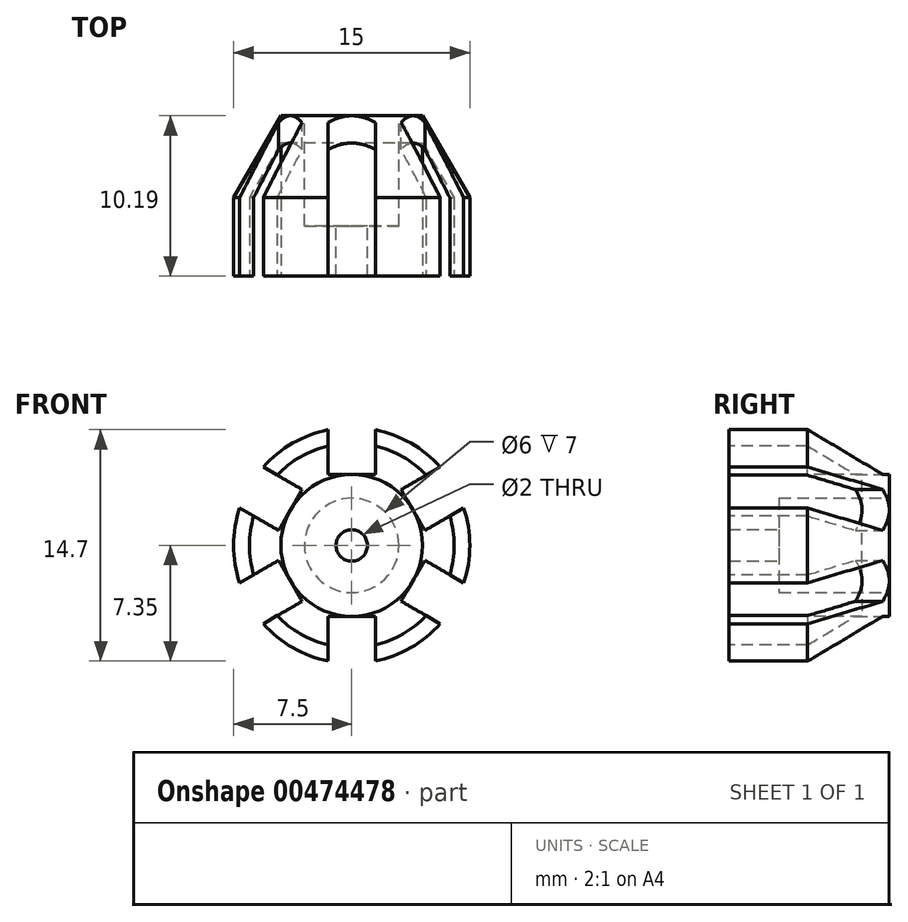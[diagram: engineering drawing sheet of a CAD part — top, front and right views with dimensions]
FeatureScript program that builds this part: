
annotation { "Feature Type Name" : "Feature", "Feature Type Description" : "" }
export const myFeature = defineFeature(function(context is Context, id is Id, definition is map)
    precondition{}
    {
        {
            var Q0;
            Q0=qCreatedBy(makeId("Right.planeOp"),FACE);
            var sketch = newSketch(context, id + "F0", { "sketchPlane" : qUnion([Q0])});
            skLineSegment(sketch, "E0", {"start": v(16.88, 0) * mm, "end": v(16.88, 4.5) * mm});
            skLineSegment(sketch, "E1", {"start": v(16.88, 4.5) * mm, "end": v(11.69, 7.5) * mm});
            skLineSegment(sketch, "E2", {"start": v(11.69, 7.5) * mm, "end": v(6.69, 7.5) * mm});
            skLineSegment(sketch, "E3", {"start": v(6.69, 7.5) * mm, "end": v(6.69, 6.5) * mm});
            skLineSegment(sketch, "E4", {"start": v(6.69, 6.5) * mm, "end": v(11.69, 6.5) * mm});
            skLineSegment(sketch, "E5", {"start": v(11.69, 6.5) * mm, "end": v(15.15, 4.5) * mm});
            skLineSegment(sketch, "E6", {"start": v(15.15, 4.5) * mm, "end": v(6.69, 4.5) * mm});
            skLineSegment(sketch, "E7", {"start": v(6.69, 4.5) * mm, "end": v(6.69, 0) * mm});
            skLineSegment(sketch, "E8", {"start": v(6.69, 0) * mm, "end": v(16.88, 0) * mm});
            skLineSegment(sketch, "E9", {"start": v(0, 0) * mm, "end": v(16.88, 0) * mm, "construction": true});
            skSolve(sketch);
        }
        {
            var Q0;
            Q0 = qSketchRegion(id + "F0", true);
            var Q1;
            Q1=sQuery(id+"F0.wireOp",EDGE,"E9");
            revolve(context, id + "F1", {"entities" : qUnion([Q0]), "axis" : qUnion([Q1]), "revolveType" : RevolveType.FULL});
        }
        {
            var Q0;
            Q0=makeQuery(id+"F1.opRevolve","SWEPT_FACE",FACE,{"disambiguationData":[OSD([sQuery(id+"F0.wireOp",EDGE,"E0")])]});
            var sketch = newSketch(context, id + "F2", { "sketchPlane" : qUnion([Q0])});
            skCircle(sketch, "E10", {"center": v(0, 0) * mm, "radius": 7.5 * mm});
            skLineSegment(sketch, "E11.bottom", {"start": v(-1.5, 10.5) * mm, "end": v(1.5, 10.5) * mm});
            skLineSegment(sketch, "E11.top", {"start": v(-1.5, 4.5) * mm, "end": v(1.5, 4.5) * mm});
            skLineSegment(sketch, "E11.left", {"start": v(-1.5, 10.5) * mm, "end": v(-1.5, 4.5) * mm});
            skLineSegment(sketch, "E11.right", {"start": v(1.5, 10.5) * mm, "end": v(1.5, 4.5) * mm});
            skPoint(sketch, "E11.middle", {"position": v(0, 7.5) * mm});
            skLineSegment(sketch, "E12.1.0", {"start": v(-9.84, 3.95) * mm, "end": v(-4.65, 0.95) * mm});
            skLineSegment(sketch, "E12.1.1", {"start": v(-4.65, 0.95) * mm, "end": v(-3.15, 3.55) * mm});
            skLineSegment(sketch, "E12.1.2", {"start": v(-8.34, 6.55) * mm, "end": v(-3.15, 3.55) * mm});
            skLineSegment(sketch, "E12.1.3", {"start": v(-9.84, 3.95) * mm, "end": v(-8.34, 6.55) * mm});
            skLineSegment(sketch, "E12.2.0", {"start": v(-8.34, -6.55) * mm, "end": v(-3.15, -3.55) * mm});
            skLineSegment(sketch, "E12.2.1", {"start": v(-3.15, -3.55) * mm, "end": v(-4.65, -0.95) * mm});
            skLineSegment(sketch, "E12.2.2", {"start": v(-9.84, -3.95) * mm, "end": v(-4.65, -0.95) * mm});
            skLineSegment(sketch, "E12.2.3", {"start": v(-8.34, -6.55) * mm, "end": v(-9.84, -3.95) * mm});
            skLineSegment(sketch, "E12.3.0", {"start": v(1.5, -10.5) * mm, "end": v(1.5, -4.5) * mm});
            skLineSegment(sketch, "E12.3.1", {"start": v(1.5, -4.5) * mm, "end": v(-1.5, -4.5) * mm});
            skLineSegment(sketch, "E12.3.2", {"start": v(-1.5, -10.5) * mm, "end": v(-1.5, -4.5) * mm});
            skLineSegment(sketch, "E12.3.3", {"start": v(1.5, -10.5) * mm, "end": v(-1.5, -10.5) * mm});
            skLineSegment(sketch, "E12.4.0", {"start": v(9.84, -3.95) * mm, "end": v(4.65, -0.95) * mm});
            skLineSegment(sketch, "E12.4.1", {"start": v(4.65, -0.95) * mm, "end": v(3.15, -3.55) * mm});
            skLineSegment(sketch, "E12.4.2", {"start": v(8.34, -6.55) * mm, "end": v(3.15, -3.55) * mm});
            skLineSegment(sketch, "E12.4.3", {"start": v(9.84, -3.95) * mm, "end": v(8.34, -6.55) * mm});
            skLineSegment(sketch, "E12.5.0", {"start": v(8.34, 6.55) * mm, "end": v(3.15, 3.55) * mm});
            skLineSegment(sketch, "E12.5.1", {"start": v(3.15, 3.55) * mm, "end": v(4.65, 0.95) * mm});
            skLineSegment(sketch, "E12.5.2", {"start": v(9.84, 3.95) * mm, "end": v(4.65, 0.95) * mm});
            skLineSegment(sketch, "E12.5.3", {"start": v(8.34, 6.55) * mm, "end": v(9.84, 3.95) * mm});
            skSolve(sketch);
        }
        {
            var Q0;
            {var subQ0=sQuery(id+"F2.wireOp",EDGE,"E12.2.2");var subQ6=sQuery(id+"F2.wireOp",EDGE,"E10");var subQ7=makeQuery(id+"F2.imprint","INTERSECT",VERTEX,{"derivedFrom":[subQ6,subQ0]});Q0=makeQuery(id+"F2.imprint","IMPRINT",FACE,{"disambiguationData":[TD([[makeQuery(id+"F2.imprint","IMPRINT",EDGE,{"disambiguationData":[TD([[subQ7,-1.0]])],"derivedFrom":subQ6}),1.0]])]});}
            var Q1;
            {var subQ0=sQuery(id+"F2.wireOp",EDGE,"E12.1.2");var subQ6=sQuery(id+"F2.wireOp",EDGE,"E10");var subQ8=makeQuery(id+"F2.imprint","INTERSECT",VERTEX,{"derivedFrom":[subQ6,subQ0]});Q1=makeQuery(id+"F2.imprint","IMPRINT",FACE,{"disambiguationData":[TD([[makeQuery(id+"F2.imprint","IMPRINT",EDGE,{"disambiguationData":[TD([[subQ8,-1.0]])],"derivedFrom":subQ6}),1.0]])]});}
            var Q2;
            {var subQ3=sQuery(id+"F2.wireOp",EDGE,"E10");var subQ5=sQuery(id+"F2.wireOp",EDGE,"E11.right");var subQ8=makeQuery(id+"F2.imprint","INTERSECT",VERTEX,{"derivedFrom":[subQ3,subQ5]});Q2=makeQuery(id+"F2.imprint","IMPRINT",FACE,{"disambiguationData":[TD([[makeQuery(id+"F2.imprint","IMPRINT",EDGE,{"disambiguationData":[TD([[subQ8,-1.0]])],"derivedFrom":subQ3}),1.0]])]});}
            var Q3;
            {var subQ1=sQuery(id+"F2.wireOp",EDGE,"E12.5.0");var subQ4=sQuery(id+"F2.wireOp",EDGE,"E10");var subQ5=makeQuery(id+"F2.imprint","INTERSECT",VERTEX,{"derivedFrom":[subQ4,subQ1]});Q3=makeQuery(id+"F2.imprint","IMPRINT",FACE,{"disambiguationData":[TD([[makeQuery(id+"F2.imprint","IMPRINT",EDGE,{"disambiguationData":[TD([[subQ5,1.0]])],"derivedFrom":subQ4}),1.0]])]});}
            var Q4;
            {var subQ0=sQuery(id+"F2.wireOp",EDGE,"E12.4.2");var subQ4=sQuery(id+"F2.wireOp",EDGE,"E10");var subQ5=makeQuery(id+"F2.imprint","INTERSECT",VERTEX,{"derivedFrom":[subQ4,subQ0]});Q4=makeQuery(id+"F2.imprint","IMPRINT",FACE,{"disambiguationData":[TD([[makeQuery(id+"F2.imprint","IMPRINT",EDGE,{"disambiguationData":[TD([[subQ5,-1.0]])],"derivedFrom":subQ4}),1.0]])]});}
            var Q5;
            {var subQ0=sQuery(id+"F2.wireOp",EDGE,"E12.3.2");var subQ6=sQuery(id+"F2.wireOp",EDGE,"E10");var subQ8=makeQuery(id+"F2.imprint","INTERSECT",VERTEX,{"derivedFrom":[subQ6,subQ0]});Q5=makeQuery(id+"F2.imprint","IMPRINT",FACE,{"disambiguationData":[TD([[makeQuery(id+"F2.imprint","IMPRINT",EDGE,{"disambiguationData":[TD([[subQ8,-1.0]])],"derivedFrom":subQ6}),1.0]])]});}
            var Q6;
            Q6=makeQuery(id+"F2.imprint","IMPRINT",FACE,{"disambiguationData":[TD([[makeQuery(id+"F2.imprint","IMPRINT",EDGE,{"derivedFrom":sQuery(id+"F2.wireOp",EDGE,"XF7wWJKb-Ourd-CVz5-kIUM-uNinxLY8hfD8")}),1.0]])]});
            extrude(context, id + "F3", {"entities" : qUnion([Q0, Q1, Q2, Q3, Q4, Q5, Q6]), "operationType" : NewBodyOperationType.REMOVE, "oppositeDirection" : true, "depth" : 25 * mm});
        }
        {
            var Q0;
            Q0=makeQuery(id+"F1.opRevolve","SWEPT_FACE",FACE,{"disambiguationData":[OSD([sQuery(id+"F0.wireOp",EDGE,"E0")])]});
            var sketch = newSketch(context, id + "F4", { "sketchPlane" : qUnion([Q0])});
            skCircle(sketch, "E13", {"center": v(0, 0) * mm, "radius": 3 * mm});
            skSolve(sketch);
        }
        {
            var Q0;
            Q0 = qSketchRegion(id + "F4", true);
            extrude(context, id + "F5", {"entities" : qUnion([Q0]), "operationType" : NewBodyOperationType.REMOVE, "oppositeDirection" : true, "depth" : 7 * mm});
        }
        {
            var Q0;
            Q0=makeQuery(id+"F5.boolean.opBoolean","COPY",FACE,{"derivedFrom":makeQuery(id+"F5.opExtrude","CAP_FACE",FACE,{"disambiguationData":[OSD([sQuery(id+"F4.wireOp",EDGE,"E13")])],"isStart":false})});
            var sketch = newSketch(context, id + "F6", { "sketchPlane" : qUnion([Q0])});
            skCircle(sketch, "E14", {"center": v(0, 0) * mm, "radius": 1 * mm});
            skSolve(sketch);
        }
        {
            var Q0;
            Q0=makeQuery(id+"F6.imprint","IMPRINT",FACE,{"disambiguationData":[TD([[makeQuery(id+"F6.imprint","IMPRINT",EDGE,{"derivedFrom":sQuery(id+"F6.wireOp",EDGE,"E14")}),1.0]])]});
            extrude(context, id + "F7", {"entities" : qUnion([Q0]), "operationType" : NewBodyOperationType.REMOVE, "oppositeDirection" : true, "depth" : 25 * mm});
        }
    });
